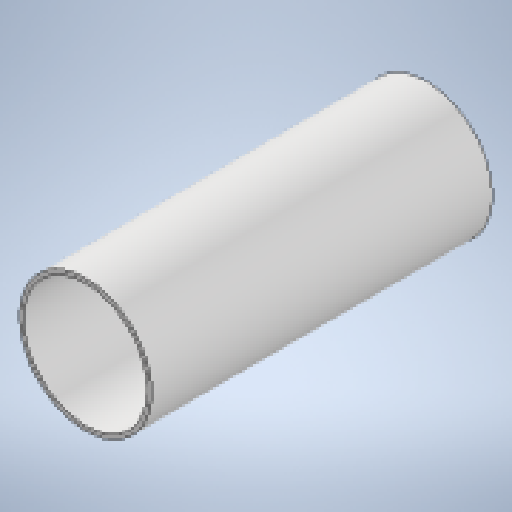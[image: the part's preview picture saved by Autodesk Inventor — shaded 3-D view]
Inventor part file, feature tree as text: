
AUTODESK INVENTOR PART (.ipt)
format: ipt  version: 2025.1 (Build 291241020, 241B)  size: 142,848 bytes
history: native  units: mm
features: extrude x1, sketch x1
ambient origin geometry x8: Origin, YZ Plane, XZ Plane, XY Plane, X Axis, Y Axis, Z Axis, Center Point
bodies: Solid1 (feature_tree)
feature tree (2):
  extrude  "Extrusion1"  Depth=232.0mm
  sketch  "Sketch1"  dims[d0=90.0mm d1=3.0mm d2=232.0mm d3=0.0mm]
